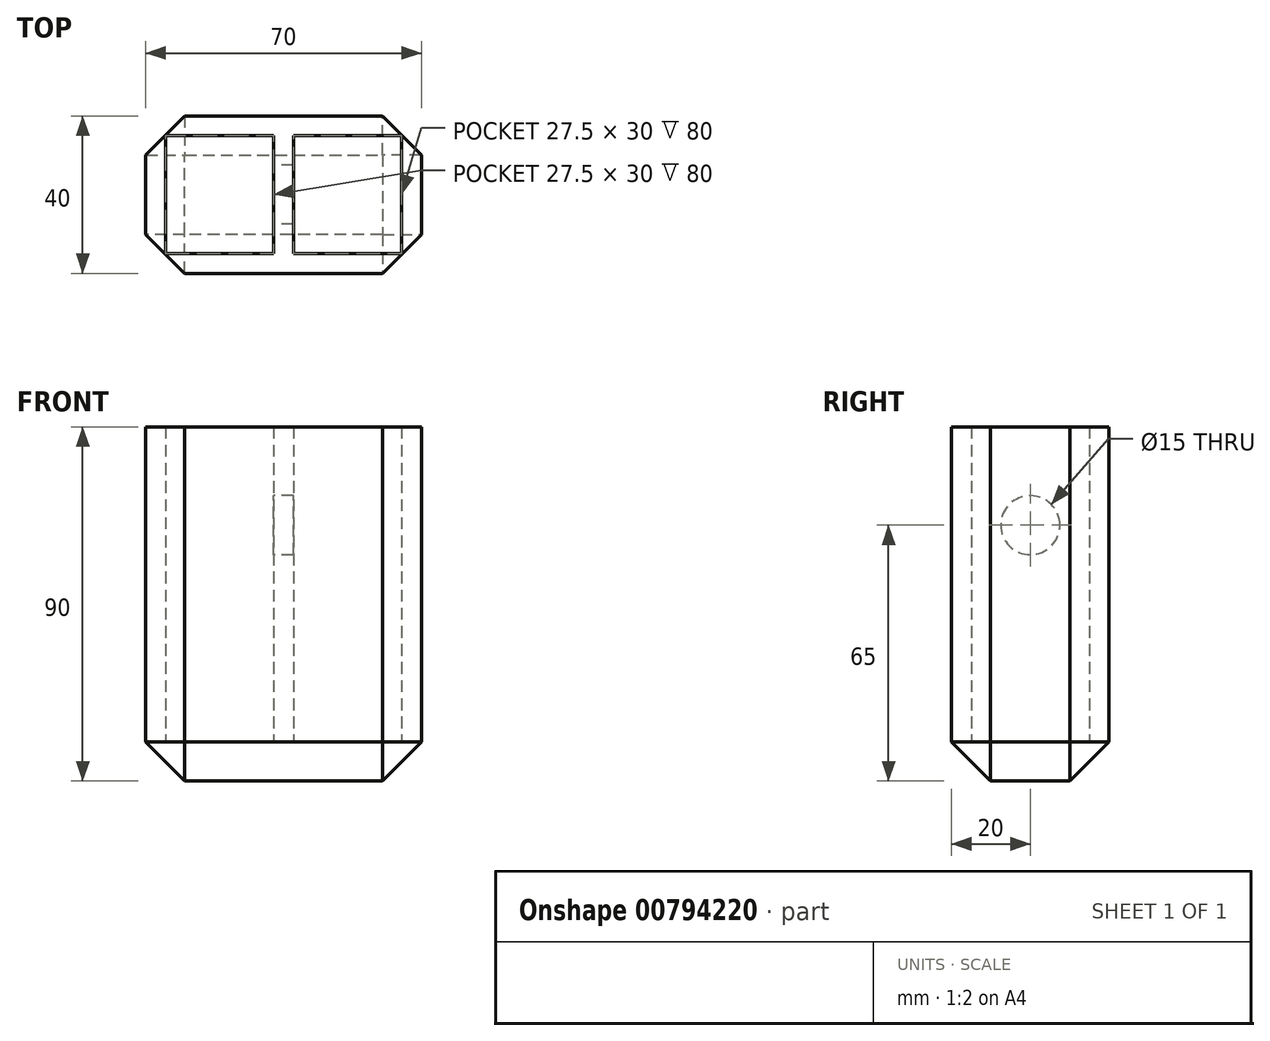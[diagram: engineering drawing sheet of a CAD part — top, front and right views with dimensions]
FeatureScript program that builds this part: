
annotation { "Feature Type Name" : "Feature", "Feature Type Description" : "" }
export const myFeature = defineFeature(function(context is Context, id is Id, definition is map)
    precondition{}
    {
        {
            var Q0;
            Q0=qCreatedBy(makeId("Top.planeOp"),FACE);
            var sketch = newSketch(context, id + "F0", { "sketchPlane" : qUnion([Q0])});
            skLineSegment(sketch, "E0.bottom", {"start": v(-35, 20) * mm, "end": v(35, 20) * mm});
            skLineSegment(sketch, "E0.top", {"start": v(-35, -20) * mm, "end": v(35, -20) * mm});
            skLineSegment(sketch, "E0.left", {"start": v(-35, 20) * mm, "end": v(-35, -20) * mm});
            skLineSegment(sketch, "E0.right", {"start": v(35, 20) * mm, "end": v(35, -20) * mm});
            skLineSegment(sketch, "E1.bottom", {"start": v(-30, 15) * mm, "end": v(30, 15) * mm});
            skLineSegment(sketch, "E1.top", {"start": v(-30, -15) * mm, "end": v(30, -15) * mm});
            skLineSegment(sketch, "E1.left", {"start": v(-30, 15) * mm, "end": v(-30, -15) * mm});
            skLineSegment(sketch, "E1.right", {"start": v(30, 15) * mm, "end": v(30, -15) * mm});
            skLineSegment(sketch, "E2", {"start": v(-2.5, 15) * mm, "end": v(-2.5, -15) * mm});
            skLineSegment(sketch, "E3", {"start": v(2.5, 15) * mm, "end": v(2.5, -15) * mm});
            skPoint(sketch, "E4.end.orphan", {"position": v(-2.5, 0) * mm});
            skPoint(sketch, "E5.end.orphan", {"position": v(2.5, 0) * mm});
            skSolve(sketch);
        }
        {
            var Q0;
            Q0=qCreatedBy(makeId("Right.planeOp"),FACE);
            var sketch = newSketch(context, id + "F1", { "sketchPlane" : qUnion([Q0])});
            skCircle(sketch, "E6", {"center": v(0, 65) * mm, "radius": 7.5 * mm});
            skSolve(sketch);
        }
        {
            var Q0;
            {var subQ0=sQuery(id+"F0.wireOp",EDGE,"E2");Q0=makeQuery(id+"F0.imprint","IMPRINT",FACE,{"disambiguationData":[TD([[makeQuery(id+"F0.imprint","IMPRINT",EDGE,{"derivedFrom":subQ0}),1.0]])]});}
            extrude(context, id + "F2", {"entities" : qUnion([Q0]), "depth" : 90 * mm, "offsetDistance" : 25 * mm});
        }
        {
            var Q0;
            Q0=makeQuery(id+"F0.imprint","IMPRINT",FACE,{"disambiguationData":[TD([[makeQuery(id+"F0.imprint","IMPRINT",EDGE,{"derivedFrom":sQuery(id+"F0.wireOp",EDGE,"E0.bottom")}),-1.0]])]});
            extrude(context, id + "F3", {"entities" : qUnion([Q0]), "operationType" : NewBodyOperationType.ADD, "depth" : 90 * mm, "offsetDistance" : 25 * mm});
        }
        {
            var Q0;
            {var subQ0=sQuery(id+"F0.wireOp",EDGE,"E1.left");Q0=makeQuery(id+"F0.imprint","IMPRINT",FACE,{"disambiguationData":[TD([[makeQuery(id+"F0.imprint","IMPRINT",EDGE,{"derivedFrom":subQ0}),1.0]])]});}
            var Q1;
            {var subQ0=sQuery(id+"F0.wireOp",EDGE,"E1.right");Q1=makeQuery(id+"F0.imprint","IMPRINT",FACE,{"disambiguationData":[TD([[makeQuery(id+"F0.imprint","IMPRINT",EDGE,{"derivedFrom":subQ0}),-1.0]])]});}
            extrude(context, id + "F4", {"entities" : qUnion([Q0, Q1]), "operationType" : NewBodyOperationType.ADD, "depth" : 10 * mm, "offsetDistance" : 25 * mm});
        }
        {
            var Q0;
            Q0=qSketchRegion(id+"F1",true);
            extrude(context, id + "F5", {"entities" : qUnion([Q0]), "operationType" : NewBodyOperationType.REMOVE, "depth" : 15 * mm, "offsetDistance" : 25 * mm, "hasSecondDirection" : true, "secondDirectionOppositeDirection" : true, "secondDirectionDepth" : 25 * mm});
        }
        {
            var Q0;
            Q0=makeQuery(id+"F3.opExtrude","SWEPT_EDGE",EDGE,{"disambiguationData":[OSD([sQuery(id+"F0.wireOp",EDGE,"E0.top"),sQuery(id+"F0.wireOp",EDGE,"E0.right")])]});
            var Q1;
            Q1=makeQuery(id+"F3.opExtrude","SWEPT_EDGE",EDGE,{"disambiguationData":[OSD([sQuery(id+"F0.wireOp",EDGE,"E0.bottom"),sQuery(id+"F0.wireOp",EDGE,"E0.right")])]});
            var Q2;
            Q2=makeQuery(id+"F3.opExtrude","SWEPT_EDGE",EDGE,{"disambiguationData":[OSD([sQuery(id+"F0.wireOp",EDGE,"E0.bottom"),sQuery(id+"F0.wireOp",EDGE,"E0.left")])]});
            var Q3;
            Q3=makeQuery(id+"F3.opExtrude","SWEPT_EDGE",EDGE,{"disambiguationData":[OSD([sQuery(id+"F0.wireOp",EDGE,"E0.top"),sQuery(id+"F0.wireOp",EDGE,"E0.left")])]});
            var Q4;
            Q4=makeQuery(id+"F3.opExtrude","CAP_EDGE",EDGE,{"disambiguationData":[OSD([sQuery(id+"F0.wireOp",EDGE,"E0.bottom")])],"isStart":true});
            var Q5;
            Q5=makeQuery(id+"F3.opExtrude","CAP_EDGE",EDGE,{"disambiguationData":[OSD([sQuery(id+"F0.wireOp",EDGE,"E0.right")])],"isStart":true});
            var Q6;
            Q6=makeQuery(id+"F3.opExtrude","CAP_EDGE",EDGE,{"disambiguationData":[OSD([sQuery(id+"F0.wireOp",EDGE,"E0.top")])],"isStart":true});
            var Q7;
            Q7=makeQuery(id+"F3.opExtrude","CAP_EDGE",EDGE,{"disambiguationData":[OSD([sQuery(id+"F0.wireOp",EDGE,"E0.left")])],"isStart":true});
            chamfer(context, id + "F6", {"entities" : qUnion([Q0, Q1, Q2, Q3, Q4, Q5, Q6, Q7]), "width" : 9.9 * mm, "tangentPropagation" : true});
        }
    });
